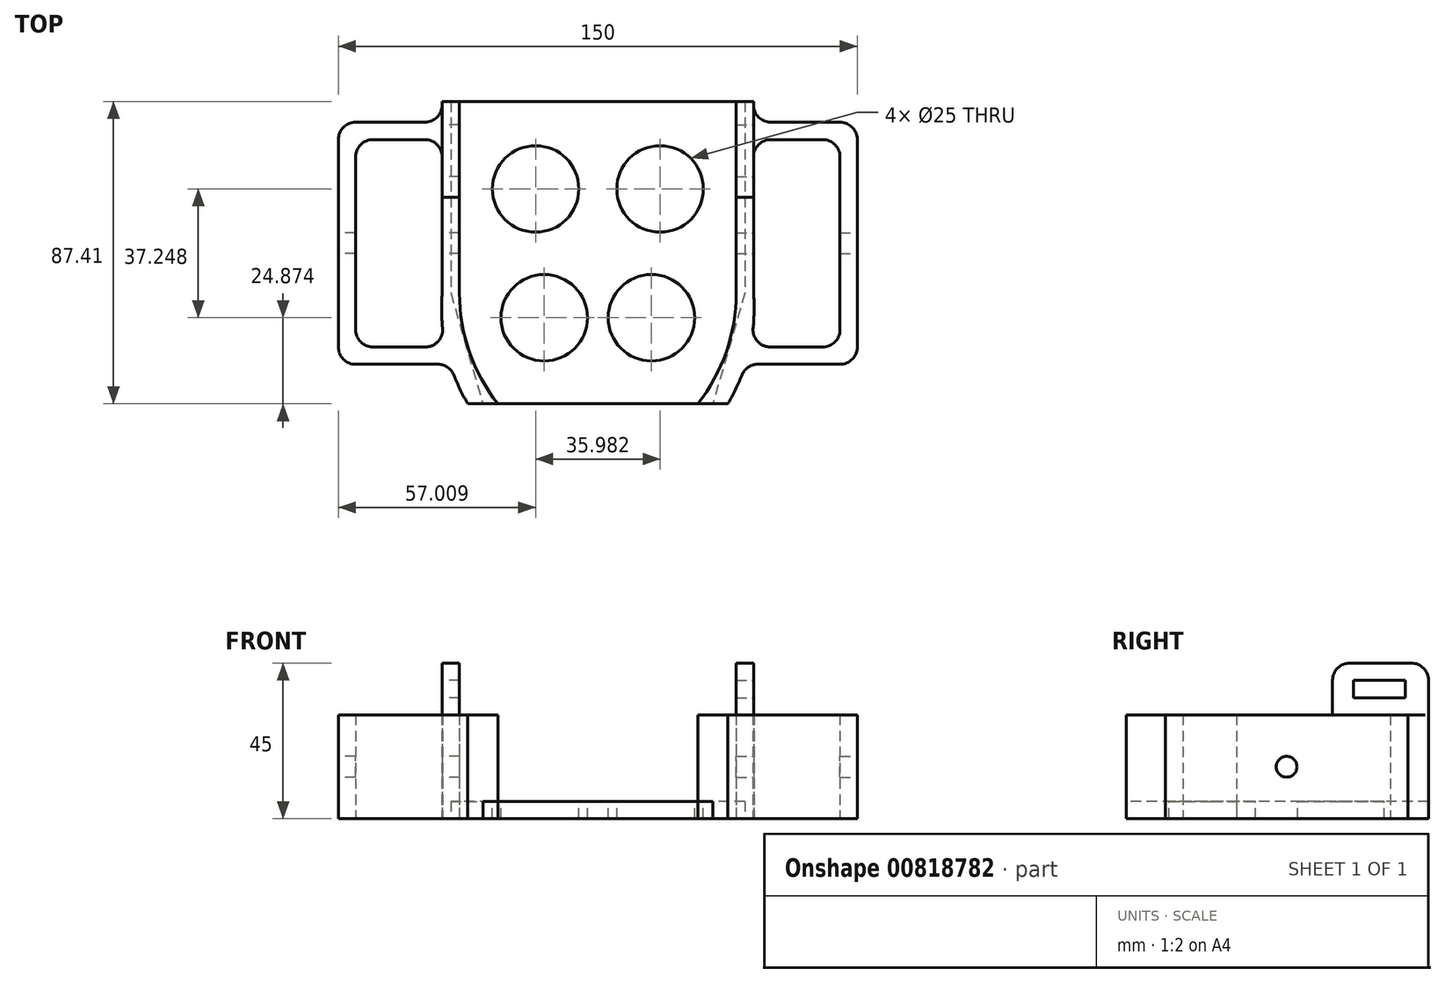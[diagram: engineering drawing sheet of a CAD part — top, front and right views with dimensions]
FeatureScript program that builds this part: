
annotation { "Feature Type Name" : "Feature", "Feature Type Description" : "" }
export const myFeature = defineFeature(function(context is Context, id is Id, definition is map)
    precondition{}
    {
        {
            var Q0;
            Q0=qCreatedBy(makeId("Top.planeOp"),FACE);
            var sketch = newSketch(context, id + "F0", { "sketchPlane" : qUnion([Q0])});
            skArc(sketch, "E0", {"start": v(-45, 0) * mm, "mid": v(-43.78, -16.56) * mm, "end": v(-37.6, -31.97) * mm});
            skLineSegment(sketch, "E1", {"start": v(-45, 0) * mm, "end": v(-45, 55.44) * mm});
            skLineSegment(sketch, "E2", {"start": v(-45, 49.44) * mm, "end": v(-75, 49.44) * mm});
            skLineSegment(sketch, "E3", {"start": v(-75, 49.44) * mm, "end": v(-75, -20.56) * mm});
            skLineSegment(sketch, "E4", {"start": v(-75, -20.56) * mm, "end": v(-42.7, -20.56) * mm});
            skLineSegment(sketch, "E5", {"start": v(-45, 44.44) * mm, "end": v(-70, 44.44) * mm});
            skLineSegment(sketch, "E6", {"start": v(-70, 44.44) * mm, "end": v(-70, -15.56) * mm});
            skLineSegment(sketch, "E7", {"start": v(-70, -15.56) * mm, "end": v(-44, -15.56) * mm});
            skLineSegment(sketch, "E8.MirrorCS", {"start": v(45, 0) * mm, "end": v(45, 55.44) * mm});
            skArc(sketch, "E9.MirrorCS", {"start": v(45, 0) * mm, "mid": v(43.78, -16.56) * mm, "end": v(37.6, -31.97) * mm});
            skLineSegment(sketch, "E10.MirrorCS", {"start": v(70, -15.56) * mm, "end": v(44, -15.56) * mm});
            skLineSegment(sketch, "E11.MirrorCS", {"start": v(75, -20.56) * mm, "end": v(42.7, -20.56) * mm});
            skLineSegment(sketch, "E12.MirrorCS", {"start": v(75, 49.44) * mm, "end": v(75, -20.56) * mm});
            skLineSegment(sketch, "E13.MirrorCS", {"start": v(70, 44.44) * mm, "end": v(70, -15.56) * mm});
            skLineSegment(sketch, "E14.MirrorCS", {"start": v(45, 44.44) * mm, "end": v(70, 44.44) * mm});
            skLineSegment(sketch, "E15.MirrorCS", {"start": v(45, 49.44) * mm, "end": v(75, 49.44) * mm});
            skLineSegment(sketch, "E16", {"start": v(-40, 55.44) * mm, "end": v(-40, 0) * mm});
            skArc(sketch, "E17", {"start": v(-40, 0) * mm, "mid": v(-37.14, -16.92) * mm, "end": v(-28.89, -31.97) * mm});
            skLineSegment(sketch, "E18.MirrorCS", {"start": v(40, 55.44) * mm, "end": v(40, 0) * mm});
            skArc(sketch, "E19.MirrorCS", {"start": v(40, 0) * mm, "mid": v(37.14, -16.92) * mm, "end": v(28.89, -31.97) * mm});
            skLineSegment(sketch, "E20", {"start": v(-45, 55.44) * mm, "end": v(-40, 55.44) * mm});
            skLineSegment(sketch, "E21.MirrorCS", {"start": v(45, 55.44) * mm, "end": v(40, 55.44) * mm});
            skLineSegment(sketch, "E22", {"start": v(-37.6, -31.97) * mm, "end": v(-28.89, -31.97) * mm});
            skPoint(sketch, "E23.orphan", {"position": v(0, -57.67) * mm});
            skLineSegment(sketch, "E24.trimOffspring", {"start": v(28.89, -31.97) * mm, "end": v(37.6, -31.97) * mm});
            skPoint(sketch, "E25.orphan", {"position": v(0, -50.23) * mm});
            skSolve(sketch);
        }
        {
            var Q0;
            Q0 = qSketchRegion(id + "F0", true);
            extrude(context, id + "F1", {"entities" : qUnion([Q0]), "depth" : 30 * mm, "offsetDistance" : 25 * mm});
        }
        {
            var Q0;
            Q0=makeQuery(id+"F1.opExtrude","CAP_FACE",FACE,{"disambiguationData":[OSD([sQuery(id+"F0.wireOp",EDGE,"E0"),sQuery(id+"F0.wireOp",EDGE,"E1"),sQuery(id+"F0.wireOp",EDGE,"E2"),sQuery(id+"F0.wireOp",EDGE,"E3"),sQuery(id+"F0.wireOp",EDGE,"E4"),sQuery(id+"F0.wireOp",EDGE,"E5"),sQuery(id+"F0.wireOp",EDGE,"E6"),sQuery(id+"F0.wireOp",EDGE,"E7"),sQuery(id+"F0.wireOp",EDGE,"E16"),sQuery(id+"F0.wireOp",EDGE,"E17"),sQuery(id+"F0.wireOp",EDGE,"E20"),sQuery(id+"F0.wireOp",EDGE,"E22")])],"isStart":true});
            var sketch = newSketch(context, id + "F2", { "sketchPlane" : qUnion([Q0])});
            skLineSegment(sketch, "E26", {"start": v(-42.5, -55.44) * mm, "end": v(0, -55.44) * mm});
            skLineSegment(sketch, "E27", {"start": v(0, -55.44) * mm, "end": v(0, 31.97) * mm});
            skLineSegment(sketch, "E28", {"start": v(0, 31.97) * mm, "end": v(-33.24, 31.97) * mm});
            skLineSegment(sketch, "E29.MirrorCS", {"start": v(42.5, -55.44) * mm, "end": v(0, -55.44) * mm});
            skLineSegment(sketch, "E30.MirrorCS", {"start": v(0, 31.97) * mm, "end": v(33.24, 31.97) * mm});
            skLineSegment(sketch, "E31", {"start": v(-42.5, -55.44) * mm, "end": v(-42.5, 0) * mm});
            skLineSegment(sketch, "E32", {"start": v(-42.5, 0) * mm, "end": v(-33.24, 31.97) * mm});
            skLineSegment(sketch, "E33.MirrorCS", {"start": v(42.5, -55.44) * mm, "end": v(42.5, 0) * mm});
            skLineSegment(sketch, "E34.MirrorCS", {"start": v(42.5, 0) * mm, "end": v(33.24, 31.97) * mm});
            skSolve(sketch);
        }
        {
            var Q0;
            Q0 = qSketchRegion(id + "F2", true);
            extrude(context, id + "F3", {"entities" : qUnion([Q0]), "oppositeDirection" : true, "depth" : 5 * mm, "offsetDistance" : 25 * mm});
        }
        {
            var Q0;
            Q0=makeQuery(id+"F1.opExtrude","SWEPT_FACE",FACE,{"disambiguationData":[OSD([sQuery(id+"F0.wireOp",EDGE,"E12.MirrorCS")])]});
            var sketch = newSketch(context, id + "F4", { "sketchPlane" : qUnion([Q0])});
            skCircle(sketch, "E35", {"center": v(14.44, 15) * mm, "radius": 3 * mm});
            skSolve(sketch);
        }
        {
            var Q0;
            Q0 = qSketchRegion(id + "F4", true);
            extrude(context, id + "F5", {"entities" : qUnion([Q0]), "operationType" : NewBodyOperationType.REMOVE, "oppositeDirection" : true, "depth" : 35 * mm, "offsetDistance" : 25 * mm});
        }
        {
            var Q0;
            Q0=makeQuery(id+"F1.opExtrude","SWEPT_FACE",FACE,{"disambiguationData":[OSD([sQuery(id+"F0.wireOp",EDGE,"E3")])]});
            var sketch = newSketch(context, id + "F6", { "sketchPlane" : qUnion([Q0])});
            skCircle(sketch, "E36", {"center": v(-14.44, 15) * mm, "radius": 3 * mm});
            skSolve(sketch);
        }
        {
            var Q0;
            Q0 = qSketchRegion(id + "F6", true);
            extrude(context, id + "F7", {"entities" : qUnion([Q0]), "operationType" : NewBodyOperationType.REMOVE, "oppositeDirection" : true, "depth" : 35 * mm, "offsetDistance" : 25 * mm});
        }
        {
            var Q0;
            Q0=makeQuery(id+"F1.opExtrude","SWEPT_FACE",FACE,{"disambiguationData":[OSD([sQuery(id+"F0.wireOp",EDGE,"E18.MirrorCS")])]});
            var sketch = newSketch(context, id + "F8", { "sketchPlane" : qUnion([Q0])});
            skPoint(sketch, "E37.oppositeSnap0", {"position": v(-27.72, 30) * mm});
            skLineSegment(sketch, "E37.bottom", {"start": v(-55.44, 30) * mm, "end": v(-27.72, 30) * mm});
            skLineSegment(sketch, "E37.top", {"start": v(-55.44, 45) * mm, "end": v(-27.72, 45) * mm});
            skLineSegment(sketch, "E37.left", {"start": v(-55.44, 30) * mm, "end": v(-55.44, 45) * mm});
            skLineSegment(sketch, "E37.right", {"start": v(-27.72, 30) * mm, "end": v(-27.72, 45) * mm});
            skLineSegment(sketch, "E38.bottom", {"start": v(-48.74, 39.97) * mm, "end": v(-33.74, 39.97) * mm});
            skLineSegment(sketch, "E38.top", {"start": v(-48.74, 34.97) * mm, "end": v(-33.74, 34.97) * mm});
            skLineSegment(sketch, "E38.left", {"start": v(-48.74, 39.97) * mm, "end": v(-48.74, 34.97) * mm});
            skLineSegment(sketch, "E38.right", {"start": v(-33.74, 39.97) * mm, "end": v(-33.74, 34.97) * mm});
            skSolve(sketch);
        }
        {
            var Q0;
            {var subQ0=sQuery(id+"F0.wireOp",EDGE,"E1");Q0=makeQuery(id+"F1.opExtrude","SWEPT_FACE",FACE,{"disambiguationData":[OSD([subQ0]),TDD([makeQuery(id+"F0.imprint","IMPRINT",EDGE,{"disambiguationData":[TD([[makeQuery(id+"F0.imprint","INTERSECT",VERTEX,{"derivedFrom":[subQ0,sQuery(id+"F0.wireOp",EDGE,"E20")]}),1.0]])],"derivedFrom":subQ0})])]});}
            var sketch = newSketch(context, id + "F9", { "sketchPlane" : qUnion([Q0])});
            skLineSegment(sketch, "E39.bottom", {"start": v(-55.44, 45) * mm, "end": v(-27.72, 45) * mm});
            skLineSegment(sketch, "E39.top", {"start": v(-55.44, 30) * mm, "end": v(-27.72, 30) * mm});
            skLineSegment(sketch, "E39.left", {"start": v(-55.44, 45) * mm, "end": v(-55.44, 30) * mm});
            skLineSegment(sketch, "E39.right", {"start": v(-27.72, 45) * mm, "end": v(-27.72, 30) * mm});
            skLineSegment(sketch, "E40.bottom", {"start": v(-48.74, 39.97) * mm, "end": v(-33.74, 39.97) * mm});
            skLineSegment(sketch, "E40.top", {"start": v(-48.74, 34.97) * mm, "end": v(-33.74, 34.97) * mm});
            skLineSegment(sketch, "E40.left", {"start": v(-48.74, 39.97) * mm, "end": v(-48.74, 34.97) * mm});
            skLineSegment(sketch, "E40.right", {"start": v(-33.74, 39.97) * mm, "end": v(-33.74, 34.97) * mm});
            skSolve(sketch);
        }
        {
            var Q0;
            Q0 = qSketchRegion(id + "F9", true);
            extrude(context, id + "F10", {"entities" : qUnion([Q0]), "operationType" : NewBodyOperationType.ADD, "oppositeDirection" : true, "depth" : 5 * mm, "offsetDistance" : 25 * mm});
        }
        {
            var Q0;
            Q0=makeQuery(id+"F1.opExtrude","SWEPT_EDGE",EDGE,{"disambiguationData":[OSD([sQuery(id+"F0.wireOp",EDGE,"E2"),sQuery(id+"F0.wireOp",EDGE,"E3")])]});
            var Q1;
            Q1=makeQuery(id+"F1.opExtrude","SWEPT_EDGE",EDGE,{"disambiguationData":[OSD([sQuery(id+"F0.wireOp",EDGE,"E3"),sQuery(id+"F0.wireOp",EDGE,"E4")])]});
            fillet(context, id + "F11", {"entities" : qUnion([Q0, Q1]), "radius" : 5 * mm, "tangentPropagation" : true, "allowEdgeOverflow" : false});
        }
        {
            var Q0;
            Q0=makeQuery(id+"F1.opExtrude","SWEPT_EDGE",EDGE,{"disambiguationData":[OSD([sQuery(id+"F0.wireOp",EDGE,"E11.MirrorCS"),sQuery(id+"F0.wireOp",EDGE,"E12.MirrorCS")])]});
            var Q1;
            Q1=makeQuery(id+"F1.opExtrude","SWEPT_EDGE",EDGE,{"disambiguationData":[OSD([sQuery(id+"F0.wireOp",EDGE,"E12.MirrorCS"),sQuery(id+"F0.wireOp",EDGE,"E15.MirrorCS")])]});
            fillet(context, id + "F12", {"entities" : qUnion([Q0, Q1]), "radius" : 5 * mm, "tangentPropagation" : true, "allowEdgeOverflow" : false});
        }
        {
            var Q0;
            Q0=makeQuery(id+"F1.opExtrude","SWEPT_EDGE",EDGE,{"disambiguationData":[OSD([sQuery(id+"F0.wireOp",EDGE,"E13.MirrorCS"),sQuery(id+"F0.wireOp",EDGE,"E14.MirrorCS")])]});
            var Q1;
            Q1=makeQuery(id+"F1.opExtrude","SWEPT_EDGE",EDGE,{"disambiguationData":[OSD([sQuery(id+"F0.wireOp",EDGE,"E10.MirrorCS"),sQuery(id+"F0.wireOp",EDGE,"E13.MirrorCS")])]});
            var Q2;
            Q2=makeQuery(id+"F1.opExtrude","SWEPT_EDGE",EDGE,{"disambiguationData":[OSD([sQuery(id+"F0.wireOp",EDGE,"E5"),sQuery(id+"F0.wireOp",EDGE,"E6")])]});
            var Q3;
            Q3=makeQuery(id+"F1.opExtrude","SWEPT_EDGE",EDGE,{"disambiguationData":[OSD([sQuery(id+"F0.wireOp",EDGE,"E6"),sQuery(id+"F0.wireOp",EDGE,"E7")])]});
            var Q4;
            Q4=makeQuery(id+"F1.opExtrude","SWEPT_EDGE",EDGE,{"disambiguationData":[OSD([sQuery(id+"F0.wireOp",EDGE,"E1"),sQuery(id+"F0.wireOp",EDGE,"E5")])]});
            var Q5;
            Q5=makeQuery(id+"F1.opExtrude","SWEPT_EDGE",EDGE,{"disambiguationData":[OSD([sQuery(id+"F0.wireOp",EDGE,"E8.MirrorCS"),sQuery(id+"F0.wireOp",EDGE,"E14.MirrorCS")])]});
            var Q6;
            Q6=makeQuery(id+"F1.opExtrude","SWEPT_EDGE",EDGE,{"disambiguationData":[OSD([sQuery(id+"F0.wireOp",EDGE,"E9.MirrorCS"),sQuery(id+"F0.wireOp",EDGE,"E10.MirrorCS")])]});
            var Q7;
            Q7=makeQuery(id+"F1.opExtrude","SWEPT_EDGE",EDGE,{"disambiguationData":[OSD([sQuery(id+"F0.wireOp",EDGE,"E0"),sQuery(id+"F0.wireOp",EDGE,"E7")])]});
            var Q8;
            Q8=makeQuery(id+"F1.opExtrude","SWEPT_EDGE",EDGE,{"disambiguationData":[OSD([sQuery(id+"F0.wireOp",EDGE,"E9.MirrorCS"),sQuery(id+"F0.wireOp",EDGE,"E11.MirrorCS")])]});
            var Q9;
            Q9=makeQuery(id+"F1.opExtrude","SWEPT_EDGE",EDGE,{"disambiguationData":[OSD([sQuery(id+"F0.wireOp",EDGE,"E0"),sQuery(id+"F0.wireOp",EDGE,"E4")])]});
            var Q10;
            Q10=makeQuery(id+"F1.opExtrude","SWEPT_EDGE",EDGE,{"disambiguationData":[OSD([sQuery(id+"F0.wireOp",EDGE,"E8.MirrorCS"),sQuery(id+"F0.wireOp",EDGE,"E15.MirrorCS")])]});
            var Q11;
            Q11=makeQuery(id+"F1.opExtrude","SWEPT_EDGE",EDGE,{"disambiguationData":[OSD([sQuery(id+"F0.wireOp",EDGE,"E1"),sQuery(id+"F0.wireOp",EDGE,"E2")])]});
            var Q12;
            Q12=makeQuery(id+"F10.opExtrude","SWEPT_EDGE",EDGE,{"disambiguationData":[OSD([sQuery(id+"F9.wireOp",EDGE,"E39.top"),sQuery(id+"F9.wireOp",EDGE,"E39.right")])]});
            fillet(context, id + "F13", {"entities" : qUnion([Q0, Q1, Q2, Q3, Q4, Q5, Q6, Q7, Q8, Q9, Q10, Q11, Q12]), "radius" : 5 * mm, "tangentPropagation" : true, "allowEdgeOverflow" : false});
        }
        {
            var Q0;
            Q0=makeQuery(id+"F10.opExtrude","SWEPT_EDGE",EDGE,{"disambiguationData":[OSD([sQuery(id+"F9.wireOp",EDGE,"E39.bottom"),sQuery(id+"F9.wireOp",EDGE,"E39.left")])]});
            var Q1;
            Q1=makeQuery(id+"FJua1TxrDA2uPtG_3.opExtrude","SWEPT_EDGE",EDGE,{"disambiguationData":[OSD([sQuery(id+"F8.wireOp",EDGE,"E37.top"),sQuery(id+"F8.wireOp",EDGE,"E37.left")])]});
            var Q2;
            Q2=makeQuery(id+"FJua1TxrDA2uPtG_3.opExtrude","SWEPT_EDGE",EDGE,{"disambiguationData":[OSD([sQuery(id+"F8.wireOp",EDGE,"E37.top"),sQuery(id+"F8.wireOp",EDGE,"E37.right")])]});
            var Q3;
            Q3=makeQuery(id+"F10.opExtrude","SWEPT_EDGE",EDGE,{"disambiguationData":[OSD([sQuery(id+"F9.wireOp",EDGE,"E39.bottom"),sQuery(id+"F9.wireOp",EDGE,"E39.right")])]});
            fillet(context, id + "F14", {"entities" : qUnion([Q0, Q1, Q2, Q3]), "radius" : 5 * mm, "tangentPropagation" : true, "allowEdgeOverflow" : false});
        }
        {
            var Q0;
            {var subQ0=sQuery(id+"F0.wireOp",EDGE,"E8.MirrorCS");Q0=makeQuery(id+"F1.opExtrude","SWEPT_FACE",FACE,{"disambiguationData":[OSD([subQ0]),TDD([makeQuery(id+"F0.imprint","IMPRINT",EDGE,{"disambiguationData":[TD([[makeQuery(id+"F0.imprint","INTERSECT",VERTEX,{"derivedFrom":[subQ0,sQuery(id+"F0.wireOp",EDGE,"E9.MirrorCS")]}),-1.0]])],"derivedFrom":subQ0})])]});}
            var sketch = newSketch(context, id + "F15", { "sketchPlane" : qUnion([Q0])});
            skLineSegment(sketch, "E41.bottom", {"start": v(27.72, 45) * mm, "end": v(55.44, 45) * mm});
            skLineSegment(sketch, "E41.top", {"start": v(27.72, 30) * mm, "end": v(55.44, 30) * mm});
            skLineSegment(sketch, "E41.left", {"start": v(27.72, 45) * mm, "end": v(27.72, 30) * mm});
            skLineSegment(sketch, "E41.right", {"start": v(55.44, 45) * mm, "end": v(55.44, 30) * mm});
            skLineSegment(sketch, "E42.bottom", {"start": v(33.74, 39.97) * mm, "end": v(48.74, 39.97) * mm});
            skLineSegment(sketch, "E42.top", {"start": v(33.74, 34.97) * mm, "end": v(48.74, 34.97) * mm});
            skLineSegment(sketch, "E42.left", {"start": v(33.74, 39.97) * mm, "end": v(33.74, 34.97) * mm});
            skLineSegment(sketch, "E42.right", {"start": v(48.74, 39.97) * mm, "end": v(48.74, 34.97) * mm});
            skSolve(sketch);
        }
        {
            var Q0;
            Q0 = qSketchRegion(id + "F15", true);
            extrude(context, id + "F16", {"entities" : qUnion([Q0]), "operationType" : NewBodyOperationType.ADD, "oppositeDirection" : true, "depth" : 5 * mm, "offsetDistance" : 25 * mm});
        }
        {
            var Q0;
            Q0=makeQuery(id+"F16.opExtrude","SWEPT_EDGE",EDGE,{"disambiguationData":[OSD([sQuery(id+"F15.wireOp",EDGE,"E41.bottom"),sQuery(id+"F15.wireOp",EDGE,"E41.right")])]});
            var Q1;
            Q1=makeQuery(id+"F16.opExtrude","SWEPT_EDGE",EDGE,{"disambiguationData":[OSD([sQuery(id+"F15.wireOp",EDGE,"E41.bottom"),sQuery(id+"F15.wireOp",EDGE,"E41.left")])]});
            var Q2;
            Q2=makeQuery(id+"F16.opExtrude","SWEPT_EDGE",EDGE,{"disambiguationData":[OSD([sQuery(id+"F0.wireOp",EDGE,"E8.MirrorCS"),sQuery(id+"F15.wireOp",EDGE,"E41.top"),sQuery(id+"F15.wireOp",EDGE,"E41.left")])]});
            fillet(context, id + "F17", {"entities" : qUnion([Q0, Q1, Q2]), "radius" : 5 * mm, "tangentPropagation" : true, "allowEdgeOverflow" : false});
        }
        {
            var Q0;
            Q0=makeQuery(id+"F3.opExtrude","CAP_FACE",FACE,{"disambiguationData":[OSD([sQuery(id+"F2.wireOp",EDGE,"E26"),sQuery(id+"F2.wireOp",EDGE,"E28"),sQuery(id+"F2.wireOp",EDGE,"E29.MirrorCS"),sQuery(id+"F2.wireOp",EDGE,"E30.MirrorCS"),sQuery(id+"F2.wireOp",EDGE,"E31"),sQuery(id+"F2.wireOp",EDGE,"E32"),sQuery(id+"F2.wireOp",EDGE,"E33.MirrorCS"),sQuery(id+"F2.wireOp",EDGE,"E34.MirrorCS")])],"isStart":false});
            var sketch = newSketch(context, id + "F18", { "sketchPlane" : qUnion([Q0])});
            skCircle(sketch, "E43", {"center": v(-18, 30.15) * mm, "radius": 12.5 * mm});
            skCircle(sketch, "E44", {"center": v(-15.5, -7.1) * mm, "radius": 12.5 * mm});
            skCircle(sketch, "E45.MirrorC", {"center": v(18, 30.15) * mm, "radius": 12.5 * mm});
            skCircle(sketch, "E46.MirrorC", {"center": v(15.5, -7.1) * mm, "radius": 12.5 * mm});
            skSolve(sketch);
        }
        {
            var Q0;
            Q0 = qSketchRegion(id + "F18", true);
            extrude(context, id + "F19", {"entities" : qUnion([Q0]), "operationType" : NewBodyOperationType.REMOVE, "oppositeDirection" : true, "depth" : 5 * mm, "offsetDistance" : 25 * mm});
        }
    });
